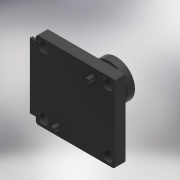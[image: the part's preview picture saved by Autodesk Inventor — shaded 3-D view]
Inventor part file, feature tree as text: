
AUTODESK INVENTOR PART (.ipt)
format: ipt  version: 2017 (Build 210142000, 142)  size: 198,656 bytes
history: native  units: mm
features: sketch x5, extrude x3, hole x1, revolve x1, fillet x1, projected_geometry x1
ambient origin geometry x8: Origin, YZ Plane, XZ Plane, XY Plane, X Axis, Y Axis, Z Axis, Center Point
bodies: Solid1 (feature_tree)
feature tree (12):
  extrude  "Extrusion1"  Depth=15.6mm
  extrude  "Extrusion2"  Depth=1.0mm
  hole  "Hole1"  [1 undecoded]
  revolve  "Revolution1"  [1 undecoded]
  fillet  "Fillet1"  Radius=13.0mm
  extrude  "Extrusion3"  Depth=1.2mm
  sketch  "Sketch1"  dims[d0=16.0mm d1=15.6mm]
  sketch  "Sketch2"  dims[d2=2.1mm d3=0.0mm d4=1.0mm]
  sketch  "Sketch3"  dims[d5=1.0mm d6=12.0mm]
  sketch  "Sketch4"  dims[d7=7.0mm d8=1.2mm d9=0.0mm d10=13.0mm]
  projected_geometry  "Projected Loop1"
  sketch  "Sketch5"  dims[d11=12.5mm d12=2.0mm d13=6.0mm d14=4.0mm d15=2.0mm d16=90.0deg d17=8.0mm d18=20.594885mm d19=9.0mm d20=6.5mm d21=7.5mm d22=0.8mm d23=1.0mm d24=13.962634mm d25=120.0deg d26=2.6mm d27=2.06mm d28=1.5mm d29=1.25mm d30=90.0deg d31=0.5mm d32=1.2mm d33=0.0mm]
note: 2 required parameter values undecoded (feature->parameter linkage not recoverable at this tier; creation-order binding heuristic only, values carry confidence <= 0.55)